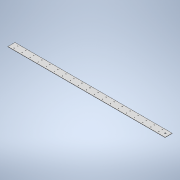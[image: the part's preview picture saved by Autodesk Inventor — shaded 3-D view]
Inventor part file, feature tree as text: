
AUTODESK INVENTOR PART (.ipt)
format: ipt  version: 2022 (Build 260153000, 153)  size: 170,496 bytes
history: native  units: mm
features: sheet_metal_op x1, sketch x1, other x1
ambient origin geometry x8: Origin, YZ Plane, XZ Plane, XY Plane, X Axis, Y Axis, Z Axis, Center Point
bodies: Body1 (feature_tree)
feature tree (3):
  sheet_metal_op  "Face4"
  sketch  "Sketch1"  dims[d0=44.0mm d1=978.0mm d2=11.0mm d3=28.0mm d4=3.35mm d5=190.0mm d7=50.0mm d8=20.0mm d10=22.0mm d16=8.0mm d17=20.0mm d18=22.0mm d19=1.5mm]
  other  "Plate4"
